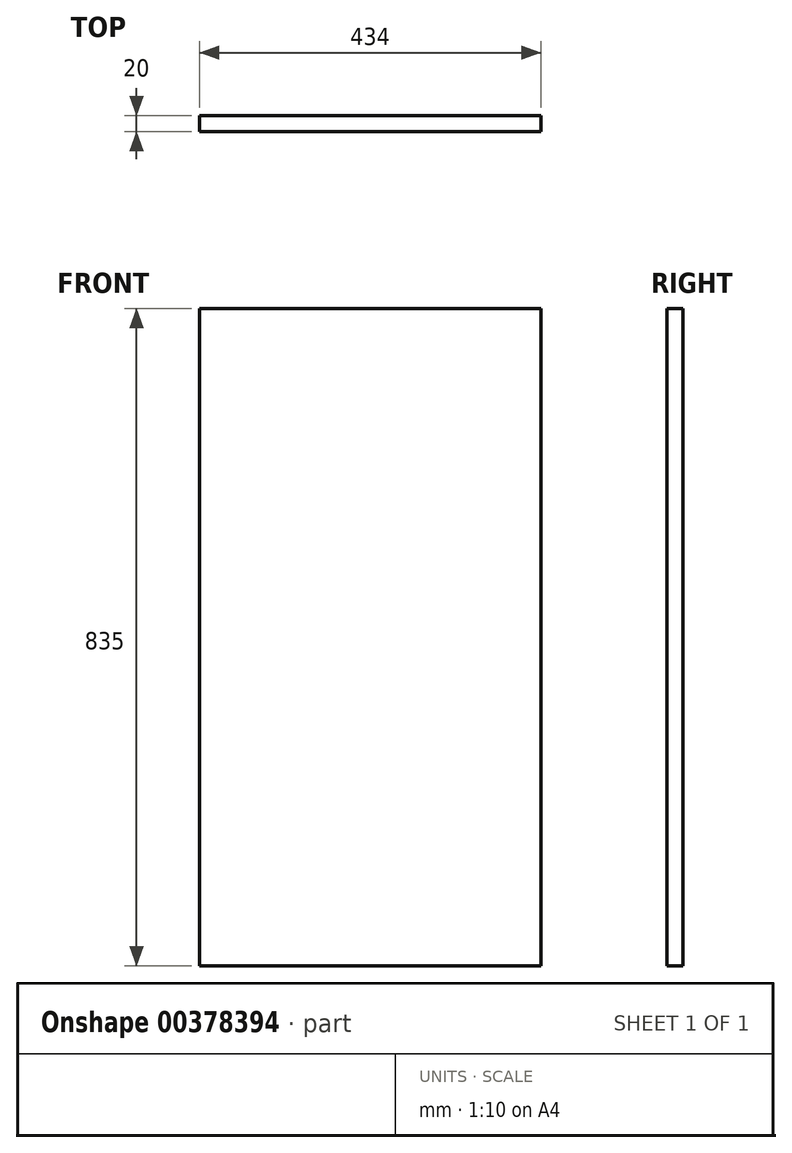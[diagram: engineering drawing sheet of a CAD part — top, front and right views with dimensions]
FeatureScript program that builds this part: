
annotation { "Feature Type Name" : "Feature", "Feature Type Description" : "" }
export const myFeature = defineFeature(function(context is Context, id is Id, definition is map)
    precondition{}
    {
        {
            var Q0;
            Q0=qCreatedBy(makeId("Front.planeOp"),FACE);
            var sketch = newSketch(context, id + "F0", { "sketchPlane" : qUnion([Q0])});
            skLineSegment(sketch, "E0.bottom", {"start": v(217, 417.5) * mm, "end": v(-217, 417.5) * mm});
            skLineSegment(sketch, "E0.top", {"start": v(217, -417.5) * mm, "end": v(-217, -417.5) * mm});
            skLineSegment(sketch, "E0.left", {"start": v(217, 417.5) * mm, "end": v(217, -417.5) * mm});
            skLineSegment(sketch, "E0.right", {"start": v(-217, 417.5) * mm, "end": v(-217, -417.5) * mm});
            skPoint(sketch, "E0.middle", {"position": v(0, 0) * mm});
            skSolve(sketch);
        }
        {
            var Q0;
            Q0 = qSketchRegion(id + "F0", true);
            extrude(context, id + "F1", {"entities" : qUnion([Q0]), "depth" : 20 * mm});
        }
    });
